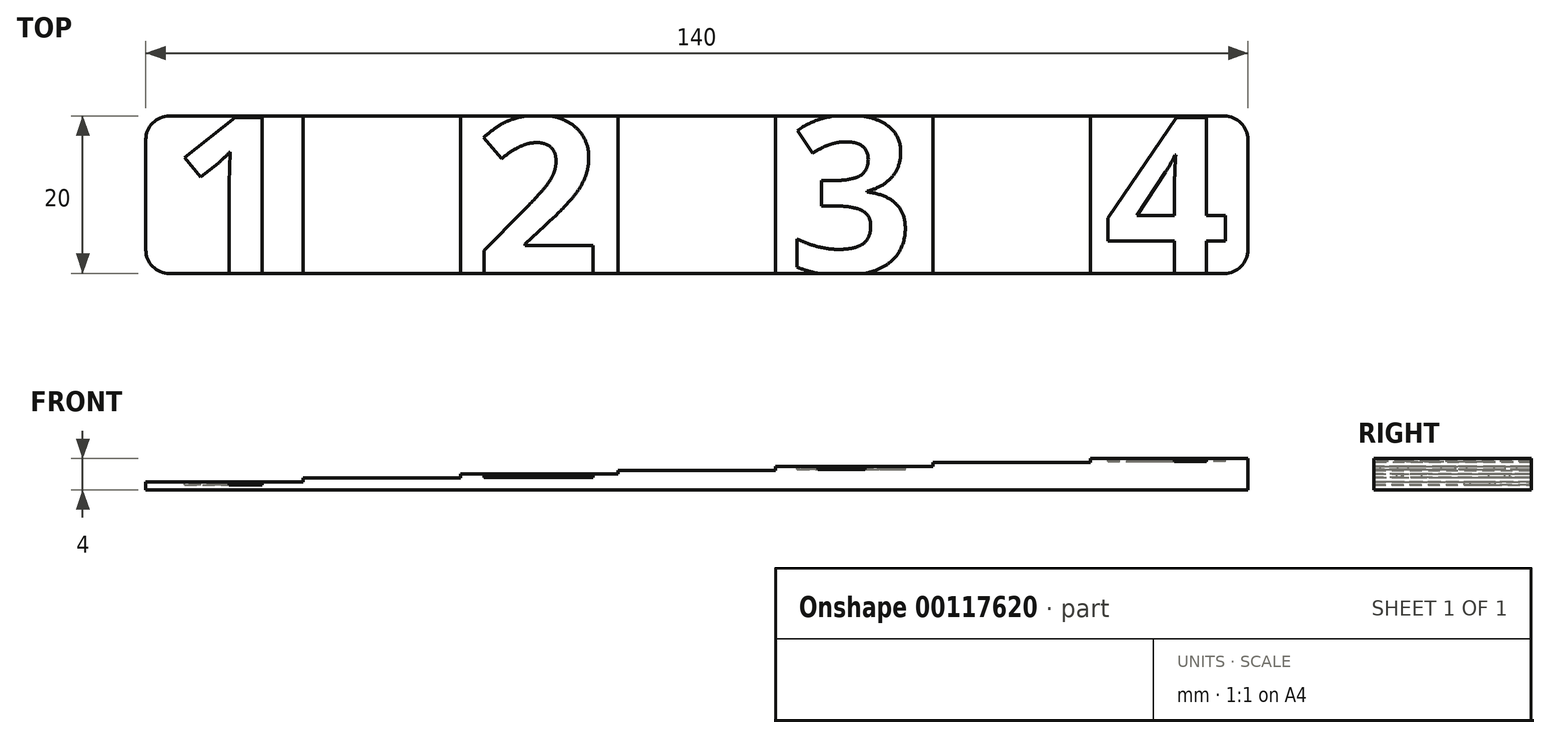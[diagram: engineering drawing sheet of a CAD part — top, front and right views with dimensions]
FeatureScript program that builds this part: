
annotation { "Feature Type Name" : "Feature", "Feature Type Description" : "" }
export const myFeature = defineFeature(function(context is Context, id is Id, definition is map)
    precondition{}
    {
        {
            var Q0;
            Q0=qCreatedBy(makeId("Top.planeOp"),FACE);
            var sketch = newSketch(context, id + "F0", { "sketchPlane" : qUnion([Q0])});
            skLineSegment(sketch, "E0.bottom", {"start": v(10, -10) * mm, "end": v(-10, -10) * mm});
            skLineSegment(sketch, "E0.top", {"start": v(10, 10) * mm, "end": v(-10, 10) * mm});
            skLineSegment(sketch, "E0.left", {"start": v(10, -10) * mm, "end": v(10, 10) * mm});
            skLineSegment(sketch, "E0.right", {"start": v(-10, -10) * mm, "end": v(-10, 10) * mm});
            skPoint(sketch, "E0.middle", {"position": v(0, 0) * mm});
            skLineSegment(sketch, "E1.bottom", {"start": v(10, -10) * mm, "end": v(30, -10) * mm});
            skLineSegment(sketch, "E1.top", {"start": v(10, 10) * mm, "end": v(30, 10) * mm});
            skLineSegment(sketch, "E1.right", {"start": v(30, -10) * mm, "end": v(30, 10) * mm});
            skLineSegment(sketch, "E2.bottom", {"start": v(30, 10) * mm, "end": v(50, 10) * mm});
            skLineSegment(sketch, "E2.top", {"start": v(30, -10) * mm, "end": v(50, -10) * mm});
            skLineSegment(sketch, "E2.left", {"start": v(30, 10) * mm, "end": v(30, -10) * mm});
            skLineSegment(sketch, "E2.right", {"start": v(50, 10) * mm, "end": v(50, -10) * mm});
            skLineSegment(sketch, "E3.bottom", {"start": v(50, 10) * mm, "end": v(70, 10) * mm});
            skLineSegment(sketch, "E3.top", {"start": v(50, -10) * mm, "end": v(70, -10) * mm});
            skLineSegment(sketch, "E3.right", {"start": v(70, 10) * mm, "end": v(70, -10) * mm});
            skLineSegment(sketch, "E4.bottom", {"start": v(70, -10) * mm, "end": v(90, -10) * mm});
            skLineSegment(sketch, "E4.top", {"start": v(70, 10) * mm, "end": v(90, 10) * mm});
            skLineSegment(sketch, "E4.left", {"start": v(70, -10) * mm, "end": v(70, 10) * mm});
            skLineSegment(sketch, "E4.right", {"start": v(90, -10) * mm, "end": v(90, 10) * mm});
            skLineSegment(sketch, "E5.bottom", {"start": v(-10, 10) * mm, "end": v(-30, 10) * mm});
            skLineSegment(sketch, "E5.top", {"start": v(-10, -10) * mm, "end": v(-30, -10) * mm});
            skLineSegment(sketch, "E5.left", {"start": v(-10, 10) * mm, "end": v(-10, -10) * mm});
            skLineSegment(sketch, "E5.right", {"start": v(-30, 10) * mm, "end": v(-30, -10) * mm});
            skLineSegment(sketch, "E6.bottom", {"start": v(-30, -10) * mm, "end": v(-50, -10) * mm});
            skLineSegment(sketch, "E6.top", {"start": v(-30, 10) * mm, "end": v(-50, 10) * mm});
            skLineSegment(sketch, "E6.left", {"start": v(-30, -10) * mm, "end": v(-30, 10) * mm});
            skLineSegment(sketch, "E6.right", {"start": v(-50, -10) * mm, "end": v(-50, 10) * mm});
            skSolve(sketch);
        }
        {
            var Q0;
            Q0=makeQuery(id+"F0.imprint","IMPRINT",FACE,{"disambiguationData":[TD([[makeQuery(id+"F0.imprint","IMPRINT",EDGE,{"derivedFrom":sQuery(id+"F0.wireOp",EDGE,"E6.bottom")}),-1.0]])]});
            extrude(context, id + "F1", {"entities" : qUnion([Q0]), "depth" : 1 * mm});
        }
        {
            var Q0;
            Q0=makeQuery(id+"F0.imprint","IMPRINT",FACE,{"disambiguationData":[TD([[makeQuery(id+"F0.imprint","IMPRINT",EDGE,{"derivedFrom":sQuery(id+"F0.wireOp",EDGE,"E5.bottom")}),1.0]])]});
            extrude(context, id + "F2", {"entities" : qUnion([Q0]), "operationType" : NewBodyOperationType.ADD, "depth" : 1.5 * mm});
        }
        {
            var Q0;
            Q0=makeQuery(id+"F0.imprint","IMPRINT",FACE,{"disambiguationData":[TD([[makeQuery(id+"F0.imprint","IMPRINT",EDGE,{"derivedFrom":sQuery(id+"F0.wireOp",EDGE,"E0.bottom")}),-1.0]])]});
            extrude(context, id + "F3", {"entities" : qUnion([Q0]), "operationType" : NewBodyOperationType.ADD, "depth" : 2 * mm});
        }
        {
            var Q0;
            Q0=makeQuery(id+"F0.imprint","IMPRINT",FACE,{"disambiguationData":[TD([[makeQuery(id+"F0.imprint","IMPRINT",EDGE,{"derivedFrom":sQuery(id+"F0.wireOp",EDGE,"E1.bottom")}),1.0]])]});
            extrude(context, id + "F4", {"entities" : qUnion([Q0]), "operationType" : NewBodyOperationType.ADD, "depth" : 2.5 * mm});
        }
        {
            var Q0;
            Q0=makeQuery(id+"F0.imprint","IMPRINT",FACE,{"disambiguationData":[TD([[makeQuery(id+"F0.imprint","IMPRINT",EDGE,{"derivedFrom":sQuery(id+"F0.wireOp",EDGE,"E2.bottom")}),-1.0]])]});
            extrude(context, id + "F5", {"entities" : qUnion([Q0]), "operationType" : NewBodyOperationType.ADD, "depth" : 3 * mm});
        }
        {
            var Q0;
            Q0=makeQuery(id+"F0.imprint","IMPRINT",FACE,{"disambiguationData":[TD([[makeQuery(id+"F0.imprint","IMPRINT",EDGE,{"derivedFrom":sQuery(id+"F0.wireOp",EDGE,"E3.bottom")}),-1.0]])]});
            extrude(context, id + "F6", {"entities" : qUnion([Q0]), "operationType" : NewBodyOperationType.ADD, "depth" : 3.5 * mm});
        }
        {
            var Q0;
            Q0=makeQuery(id+"F0.imprint","IMPRINT",FACE,{"disambiguationData":[TD([[makeQuery(id+"F0.imprint","IMPRINT",EDGE,{"derivedFrom":sQuery(id+"F0.wireOp",EDGE,"E4.bottom")}),1.0]])]});
            extrude(context, id + "F7", {"entities" : qUnion([Q0]), "operationType" : NewBodyOperationType.ADD, "depth" : 4 * mm});
        }
        {
            var Q0;
            Q0=makeQuery(id+"F1.opExtrude","CAP_FACE",FACE,{"disambiguationData":[OSD([sQuery(id+"F0.wireOp",EDGE,"E6.bottom"),sQuery(id+"F0.wireOp",EDGE,"E6.top"),sQuery(id+"F0.wireOp",EDGE,"E6.left"),sQuery(id+"F0.wireOp",EDGE,"E6.right")])],"isStart":false});
            var sketch = newSketch(context, id + "F8", { "sketchPlane" : qUnion([Q0])});
            skText(sketch, "E7", { "text": "1", "fontName": "OpenSans-Bold.ttf"});
            const initialGuessF8  = {"E7": [-0.0467, -0.01, 1, 0, 0.02]};
            skSetInitialGuess(sketch, initialGuessF8);
            skSolve(sketch);
        }
        {
            var Q0;
            Q0=makeQuery(id+"F3.opExtrude","CAP_FACE",FACE,{"disambiguationData":[OSD([sQuery(id+"F0.wireOp",EDGE,"E0.bottom"),sQuery(id+"F0.wireOp",EDGE,"E0.top"),sQuery(id+"F0.wireOp",EDGE,"E0.left"),sQuery(id+"F0.wireOp",EDGE,"E5.left")])],"isStart":false});
            var sketch = newSketch(context, id + "F9", { "sketchPlane" : qUnion([Q0])});
            skText(sketch, "E8", { "text": "2", "fontName": "OpenSans-Bold.ttf"});
            const initialGuessF9  = {"E8": [-0.00815, -0.01, 1, 0, 0.02]};
            skSetInitialGuess(sketch, initialGuessF9);
            skSolve(sketch);
        }
        {
            var Q0;
            Q0=makeQuery(id+"F5.opExtrude","CAP_FACE",FACE,{"disambiguationData":[OSD([sQuery(id+"F0.wireOp",EDGE,"E2.bottom"),sQuery(id+"F0.wireOp",EDGE,"E2.top"),sQuery(id+"F0.wireOp",EDGE,"E2.left"),sQuery(id+"F0.wireOp",EDGE,"E2.right")])],"isStart":false});
            var sketch = newSketch(context, id + "F10", { "sketchPlane" : qUnion([Q0])});
            skText(sketch, "E9", { "text": "3", "fontName": "OpenSans-Bold.ttf"});
            const initialGuessF10  = {"E9": [0.03169, -0.01, 1, 0, 0.02]};
            skSetInitialGuess(sketch, initialGuessF10);
            skSolve(sketch);
        }
        {
            var Q0;
            Q0=makeQuery(id+"F7.opExtrude","CAP_FACE",FACE,{"disambiguationData":[OSD([sQuery(id+"F0.wireOp",EDGE,"E4.bottom"),sQuery(id+"F0.wireOp",EDGE,"E4.top"),sQuery(id+"F0.wireOp",EDGE,"E4.left"),sQuery(id+"F0.wireOp",EDGE,"E4.right")])],"isStart":false});
            var sketch = newSketch(context, id + "F11", { "sketchPlane" : qUnion([Q0])});
            skText(sketch, "E10", { "text": "4", "fontName": "OpenSans-Bold.ttf"});
            const initialGuessF11  = {"E10": [0.07172, -0.01, 1, 0, 0.02]};
            skSetInitialGuess(sketch, initialGuessF11);
            skSolve(sketch);
        }
        {
            var Q0;
            Q0=makeQuery(id+"F8.imprint","IMPRINT",FACE,{"disambiguationData":[TD([[makeQuery(id+"F8.imprint","IMPRINT",EDGE,{"derivedFrom":sQuery(id+"F8.wireOp",EDGE,"E7.sketch_text.stroke-0")}),-1.0]])]});
            var Q1;
            Q1=makeQuery(id+"F10.imprint","IMPRINT",FACE,{"disambiguationData":[TD([[makeQuery(id+"F10.imprint","IMPRINT",EDGE,{"derivedFrom":sQuery(id+"F10.wireOp",EDGE,"E9.sketch_text.stroke-0")}),-1.0]])]});
            var Q2;
            Q2=makeQuery(id+"F9.imprint","IMPRINT",FACE,{"disambiguationData":[TD([[makeQuery(id+"F9.imprint","IMPRINT",EDGE,{"derivedFrom":sQuery(id+"F9.wireOp",EDGE,"E8.sketch_text.stroke-0")}),-1.0]])]});
            var Q3;
            Q3=makeQuery(id+"F11.imprint","IMPRINT",FACE,{"disambiguationData":[TD([[makeQuery(id+"F11.imprint","IMPRINT",EDGE,{"derivedFrom":sQuery(id+"F11.wireOp",EDGE,"E10.sketch_text.stroke-0")}),-1.0]])]});
            extrude(context, id + "F12", {"entities" : qUnion([Q0, Q1, Q2, Q3]), "operationType" : NewBodyOperationType.REMOVE, "oppositeDirection" : true, "depth" : 0.4 * mm});
        }
        {
            var Q0;
            Q0=makeQuery(id+"F7.opExtrude","SWEPT_EDGE",EDGE,{"disambiguationData":[OSD([sQuery(id+"F0.wireOp",EDGE,"E4.bottom"),sQuery(id+"F0.wireOp",EDGE,"E4.right")])]});
            var Q1;
            Q1=makeQuery(id+"F7.opExtrude","SWEPT_EDGE",EDGE,{"disambiguationData":[OSD([sQuery(id+"F0.wireOp",EDGE,"E4.top"),sQuery(id+"F0.wireOp",EDGE,"E4.right")])]});
            var Q2;
            Q2=makeQuery(id+"F1.opExtrude","SWEPT_EDGE",EDGE,{"disambiguationData":[OSD([sQuery(id+"F0.wireOp",EDGE,"E6.top"),sQuery(id+"F0.wireOp",EDGE,"E6.right")])]});
            var Q3;
            Q3=makeQuery(id+"F1.opExtrude","SWEPT_EDGE",EDGE,{"disambiguationData":[OSD([sQuery(id+"F0.wireOp",EDGE,"E6.bottom"),sQuery(id+"F0.wireOp",EDGE,"E6.right")])]});
            fillet(context, id + "F13", {"entities" : qUnion([Q0, Q1, Q2, Q3]), "radius" : 3 * mm, "tangentPropagation" : true, "allowEdgeOverflow" : false});
        }
    });
